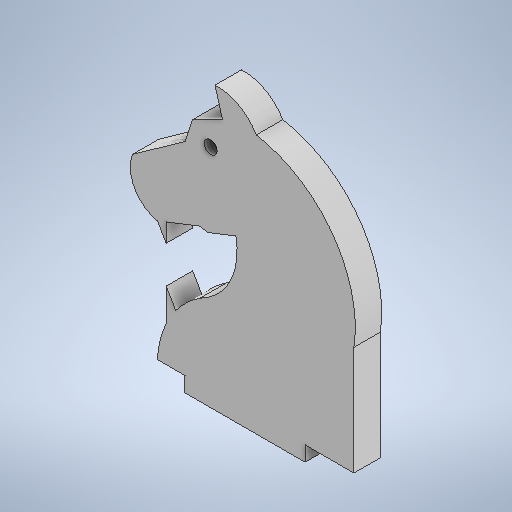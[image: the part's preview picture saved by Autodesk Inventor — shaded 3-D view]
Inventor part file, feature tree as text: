
AUTODESK INVENTOR PART (.ipt)
format: ipt  version: 2025.1 (Build 291241000, 241)  size: 311,296 bytes
history: native  units: mm
features: other x2, sketch x2, extrude x1, hole x1
ambient origin geometry x8: Origin, YZ Plane, XZ Plane, XY Plane, X Axis, Y Axis, Z Axis, Center Point
bodies: Body1 (feature_tree)
feature tree (6):
  other  "Sólido1"
  extrude  "Extrusión1"  Depth=10.0mm
  hole  "Agujero2"  [1 undecoded]
  sketch  "Boceto1"  dims[d5=10.0mm d6=0.0mm d9=14.0mm]
  other  "Imagen1"
  sketch  "Boceto3"  dims[d19=4.917mm d20=12.0mm d21=4.0mm d22=2.0mm d23=90.0deg d24=8.0mm d25=20.594885mm]
note: 1 required parameter value undecoded (feature->parameter linkage not recoverable at this tier; creation-order binding heuristic only, values carry confidence <= 0.55)
